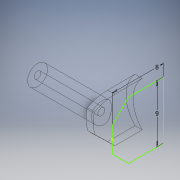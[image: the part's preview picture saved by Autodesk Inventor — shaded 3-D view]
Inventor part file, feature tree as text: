
AUTODESK INVENTOR PART (.ipt)
format: ipt  version: 2018 (Build 220112000, 112)  size: 186,368 bytes
history: native  units: mm
features: sketch x8, extrude x7, projected_geometry x1
ambient origin geometry x8: Origin, YZ Plane, XZ Plane, XY Plane, X Axis, Y Axis, Z Axis, Center Point
bodies: Solid1 (feature_tree)
feature tree (16):
  extrude  "Extrusion1"  Depth=10.0mm TaperAngle=0.0deg
  sketch  "Sketch2"  dims[d3=9.0mm d4=8.0mm d5=10.0mm d6=0.0mm]
  extrude  "Extrusion2"  Depth=10.0mm TaperAngle=0.0deg
  extrude  "Extrusion3"  Depth=1.125mm
  extrude  "Extrusion4"  Depth=0.88mm
  extrude  "Extrusion5"  Depth=0.992657mm
  extrude  "Extrusion6"  Depth=3.12mm
  extrude  "Extrusion7"  Depth=4.316mm
  sketch  "Sketch1"  dims[d0=10.0mm d1=10.0mm d2=0.0mm]
  sketch  "Sketch3"  dims[d9=1.125mm d10=1.125mm]
  sketch  "Sketch4"  dims[d12=0.0mm d13=0.0mm d16=0.88mm]
  sketch  "Sketch5"  dims[d18=0.870256mm d21=0.992657mm]
  projected_geometry  "Projected Loop1"
  sketch  "Sketch6"  dims[d23=0.992657mm d24=3.12mm]
  sketch  "Sketch7"  dims[d26=4.316mm d27=4.316mm]
  sketch  "Sketch8"  dims[d29=10.0mm d30=0.0mm d31=3.15mm d32=2.4mm d33=15.0mm d34=0.0mm d35=15.0mm d36=0.0mm d37=1.075mm d38=10.0mm d39=0.0mm]
